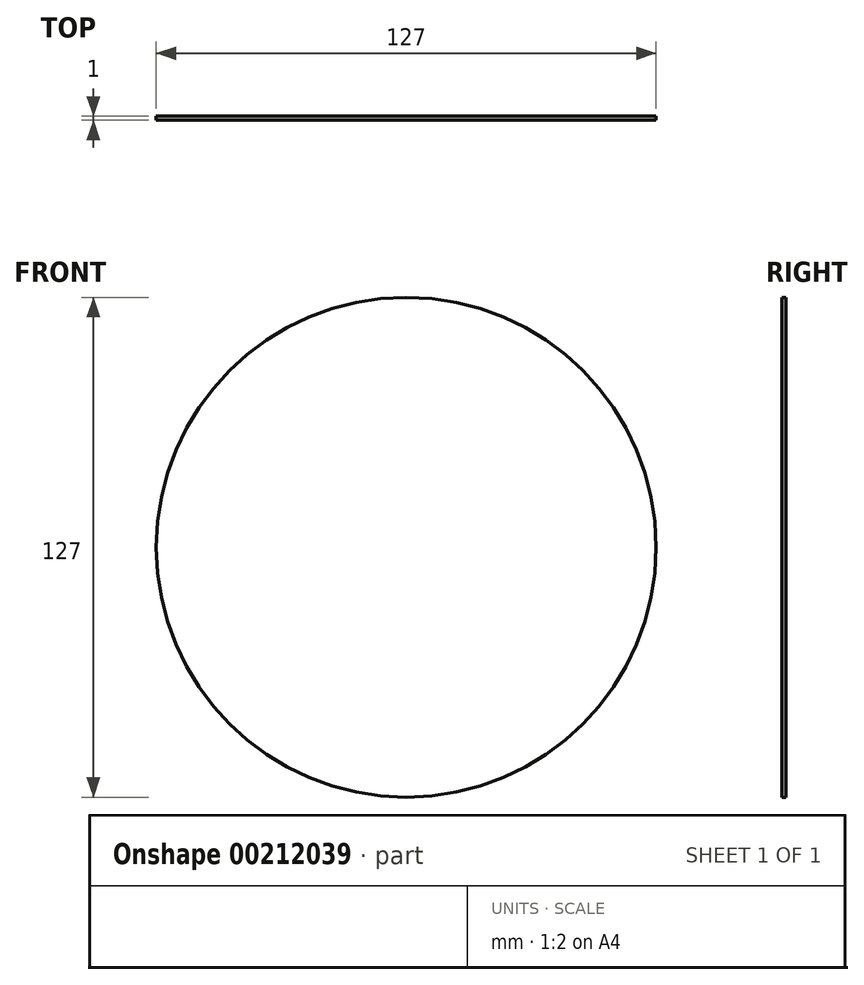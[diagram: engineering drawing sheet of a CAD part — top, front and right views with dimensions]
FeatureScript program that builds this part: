
annotation { "Feature Type Name" : "Feature", "Feature Type Description" : "" }
export const myFeature = defineFeature(function(context is Context, id is Id, definition is map)
    precondition{}
    {
        {
            var Q0;
            Q0=qCreatedBy(makeId("Front.planeOp"),FACE);
            var sketch = newSketch(context, id + "F0", { "sketchPlane" : qUnion([Q0])});
            skCircle(sketch, "E0", {"center": v(1.38, 0) * mm, "radius": 63.5 * mm});
            skSolve(sketch);
        }
        {
            var Q0;
            Q0 = qSketchRegion(id + "F0", true);
            extrude(context, id + "F1", {"entities" : qUnion([Q0]), "depth" : 1 * mm});
        }
    });
